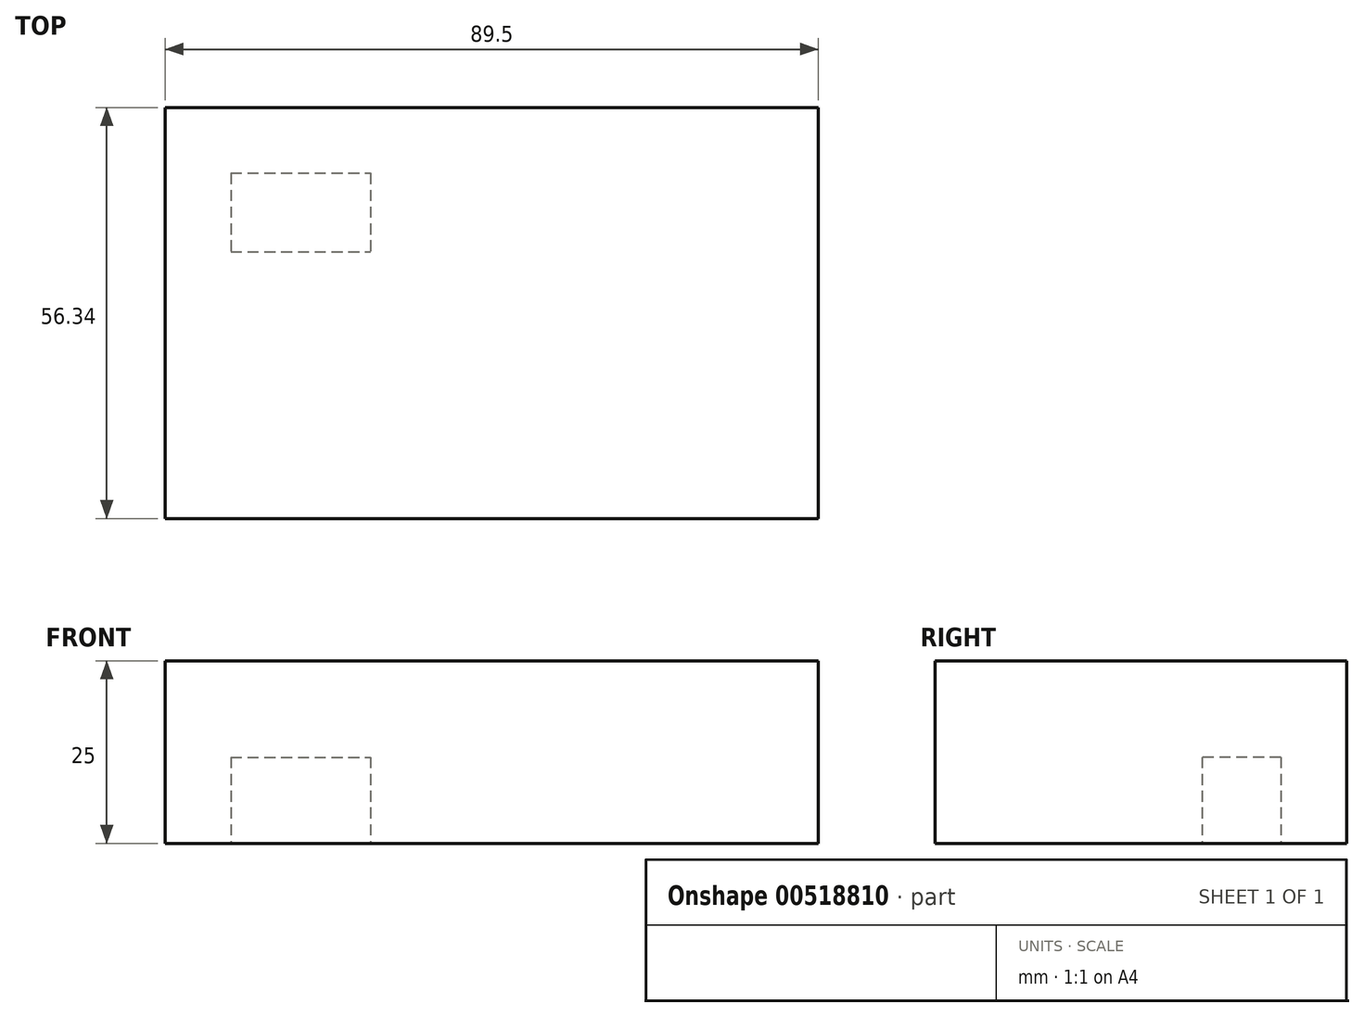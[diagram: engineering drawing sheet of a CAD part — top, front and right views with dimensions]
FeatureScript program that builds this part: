
annotation { "Feature Type Name" : "Feature", "Feature Type Description" : "" }
export const myFeature = defineFeature(function(context is Context, id is Id, definition is map)
    precondition{}
    {
        {
            var Q0;
            Q0=qCreatedBy(makeId("Top.planeOp"),FACE);
            var sketch = newSketch(context, id + "F0", { "sketchPlane" : qUnion([Q0])});
            skLineSegment(sketch, "E0.bottom", {"start": v(-44.47, 27.55) * mm, "end": v(45.03, 27.55) * mm});
            skLineSegment(sketch, "E0.top", {"start": v(-44.47, -28.79) * mm, "end": v(45.03, -28.79) * mm});
            skLineSegment(sketch, "E0.left", {"start": v(-44.47, 27.55) * mm, "end": v(-44.47, -28.79) * mm});
            skLineSegment(sketch, "E0.right", {"start": v(45.03, 27.55) * mm, "end": v(45.03, -28.79) * mm});
            skLineSegment(sketch, "E1.bottom", {"start": v(-35.47, 18.55) * mm, "end": v(-16.35, 18.55) * mm});
            skLineSegment(sketch, "E1.top", {"start": v(-35.47, 7.74) * mm, "end": v(-16.35, 7.74) * mm});
            skLineSegment(sketch, "E1.left", {"start": v(-35.47, 18.55) * mm, "end": v(-35.47, 7.74) * mm});
            skLineSegment(sketch, "E1.right", {"start": v(-16.35, 18.55) * mm, "end": v(-16.35, 7.74) * mm});
            skSolve(sketch);
        }
        {
            var Q0;
            Q0=makeQuery(id+"F0.imprint","IMPRINT",FACE,{"disambiguationData":[TD([[makeQuery(id+"F0.imprint","IMPRINT",EDGE,{"derivedFrom":sQuery(id+"F0.wireOp",EDGE,"E1.bottom")}),-1.0]])]});
            var Q1;
            Q1=makeQuery(id+"F0.imprint","IMPRINT",FACE,{"disambiguationData":[TD([[makeQuery(id+"F0.imprint","IMPRINT",EDGE,{"derivedFrom":sQuery(id+"F0.wireOp",EDGE,"E0.bottom")}),-1.0]])]});
            extrude(context, id + "F1", {"entities" : qUnion([Q0, Q1]), "depth" : 25 * mm, "offsetDistance" : 25 * mm});
        }
        {
            var Q0;
            Q0=makeQuery(id+"F0.imprint","IMPRINT",FACE,{"disambiguationData":[TD([[makeQuery(id+"F0.imprint","IMPRINT",EDGE,{"derivedFrom":sQuery(id+"F0.wireOp",EDGE,"E1.bottom")}),-1.0]])]});
            extrude(context, id + "F2", {"entities" : qUnion([Q0]), "operationType" : NewBodyOperationType.REMOVE, "depth" : 11.8 * mm, "offsetDistance" : 25 * mm});
        }
    });
